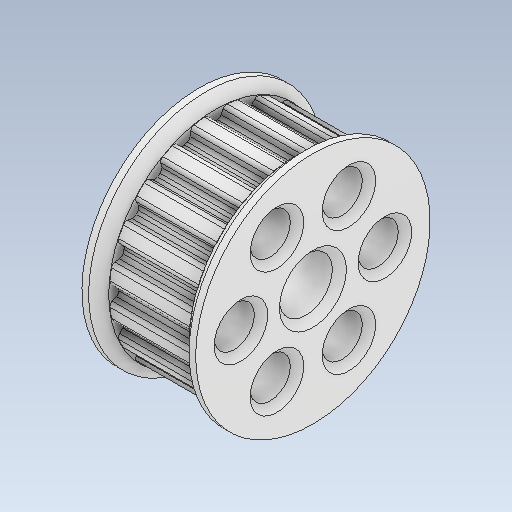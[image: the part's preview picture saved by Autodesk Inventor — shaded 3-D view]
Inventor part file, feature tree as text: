
AUTODESK INVENTOR PART (.ipt)
format: ipt  version: 2020 (Build 240168000, 168)  size: 1,069,568 bytes
history: native  units: mm
features: extrude x8, thicken_offset x8, sketch x8, projected_geometry x6, chamfer x3, plane x1, pattern_circular x1, other x1
ambient origin geometry x8: Origin, YZ Plane, XZ Plane, XY Plane, X Axis, Y Axis, Z Axis, Center Point
bodies: Solid1 (feature_tree)
feature tree (36):
  extrude  "Extrusion1"  Depth=10.0mm TaperAngle=0.0deg
  plane  "Work Plane1"
  extrude  "Extrusion2"  Depth=50.0mm
  extrude  "Extrusion3"  Depth=10.0mm TaperAngle=0.0deg
  thicken_offset  "Thicken1"
  extrude  "Extrusion5"  Depth=9.0mm
  extrude  "Extrusion6"  Depth=10.0mm TaperAngle=0.0deg
  extrude  "Extrusion7"  Depth=3.0mm TaperAngle=0.0deg
  thicken_offset  "Thicken3"
  thicken_offset  "Thicken4"
  thicken_offset  "Thicken5"
  thicken_offset  "Thicken6"
  extrude  "Extrusion9"  Depth=1.0mm
  extrude  "Extrusion10"  Depth=1.0mm
  pattern_circular  "Circular Pattern3"  [2 undecoded]
  chamfer  "Chamfer3"  Distance=0.5mm
  thicken_offset  "Thicken7"
  thicken_offset  "Thicken8"
  chamfer  "Chamfer4"  Distance=0.5mm
  chamfer  "Chamfer5"  Distance=8.0mm
  thicken_offset  "Thicken9"
  sketch  "Sketch1"  dims[d0=50.0mm d1=10.0mm d2=0.0mm]
  sketch  "Sketch2"  dims[d3=-1.0mm d4=50.0mm]
  sketch  "Sketch3"  dims[d5=10.0mm d6=0.0mm d7=10.0mm d8=0.0mm]
  projected_geometry  "Projected Loop1"
  sketch  "Sketch5"  dims[d9=9.0mm d10=9.0mm]
  projected_geometry  "Projected Loop3"
  sketch  "Sketch6"  dims[d18=6.15mm d19=10.0mm d20=0.0mm]
  projected_geometry  "Projected Loop4"
  sketch  "Sketch7"  dims[d21=36.0mm d22=3.0mm d23=0.0mm]
  projected_geometry  "Projected Loop5"
  sketch  "Sketch10"  dims[d24=3.0mm d25=0.0mm d40=1.0mm]
  projected_geometry  "Projected Loop8"
  sketch  "Sketch11"  dims[d41=1.0mm d42=1.0mm d43=1.0mm d54=0.5mm d55=0.7mm d56=0.5mm d57=0.7mm d58=8.0mm d59=25.0mm d60=0.0mm d61=6.0mm d62=25.0mm d63=0.0mm d64=60.0mm d65=62.831853mm d67=1.0mm d68=2.0mm d69=45.0deg d70=0.5mm d71=1.0mm d72=0.5mm d73=1.0mm d74=1.5mm d75=2.0mm d76=45.0deg d77=1.5mm d78=2.0mm d79=45.0deg d80=0.05mm d81=0.05mm]
  projected_geometry  "Projected Loop9"
  other  "_ATP20XL025-A-C10_b"
note: 2 required parameter values undecoded (feature->parameter linkage not recoverable at this tier; creation-order binding heuristic only, values carry confidence <= 0.55)
